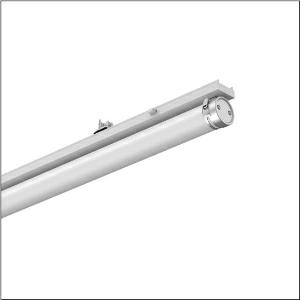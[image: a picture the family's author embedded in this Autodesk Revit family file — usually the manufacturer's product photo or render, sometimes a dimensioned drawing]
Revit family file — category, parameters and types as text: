
# Revit family: monsun_r__31_tube_51ft10mn4a0atr2_ffb0
name_source: partatom
category: Lighting Fixtures
units: mm (PartAtom-declared; Revit-internal decimal feet)

## family parameters
Cut with Voids When Loaded = No
Host = Face
Light Source = No
Part Type = Normal
Room Calculation Point = No
Round Connector Dimension = Use Diameter
Shared = No

## types (1)
- --- (1 x LED, 10000 lm, 58 W, 4000K)
    Apparent Load = 58 VA
    CIE Flux Codes = 42 71 90 91 100
    Color Rendering = 80
    Color Temperature = 4000K
    Default Elevation = 1800 mm
    Description = Monsun® 31 Tube, tubular luminaire, primary optical cover: diffuser, of PMMA, light emission: direct distribution, primary light characteristic: symmetric, LED, rated luminous flux: 10.000lm, luminous efficacy: 172lm/W, light colour: 840, colour temperature: 4000K, with with 1 terminal, 3-pole, max. 2.5mm², mains connection: 220..240V, AC, 50/60Hz, rated input power: 58W, housing, cylindrical, of PMMA, semi-transparent, matt white, with luminaire and ceiling fastening, V4A, mounting with brackets of stainless steel, length: 1.500mm, diameter: 75mm, end cap, of stainless steel (V4A), protection rating (complete): IP20, protection rating (lamp compartment): IP67/69K, insulation class (complete): insulation class I (protective earthing), certification: CE, UKCA, impact resistance: IK06, permissible operating ambient temperature: -20..+40°C, corresponds to IFS (International Featured Standards) requirements for safety and quality in the food industry, contact your sales advisor before using the luminaires in applications with unclear chemical exposure, large temperature fluctuations or condensation-forming humidity, packaging unit: 1 piece
    Height = 132 mm
    Lamp = 1 x LED
    Lamp Light Flux = 10000 lm
    Lamp Power = 58 W
    Lamp count = 1
    Length = 1500 mm
    Luminous efficacy = 172 lm/W
    Manufacturer = Siteco
    ModVariant = No
    Model = 51FT10MN4A0ATR2
    Mounting Place = Ceiling
    Mounting Type = Pendant
    Number of Poles = 1
    OnlyDefault = Yes
    Power Factor = 1
    Product Name = Monsun® 31 Tube
    Product group = tubular luminaire
    ProductGroupID = 906
    Protection Class = Protection class I
    Protection Degree = IP 20
    RLX_Detail_Level = 1
    RLX_Emergency_Light_Flux = 0 lm
    RLX_Emergency_Type = 0
    RLX_Emergency_Type_DB = No
    RlxData = <blob elided: 32245 chars, md5=8649074f>
    Socket = socket
    Standby Power = 0 W
    System Light Flux = 10000 lm
    System Power = 58 W
    Type Comments = factory setting: luminous flux: 100 % | (OFF | OFF | OFF | OFF) | 350 mA
    Type Image = l_1242814.jpg
    URL = http://relux.com
    VarID = @adj_113165
    Voltage = 0 V
    Weight = 0.00 kg
    Width = 79 mm

## geometry (parser evidence)
native form markers: Blend x4, Sweep x12
no freeform markers — native parametric forms only
